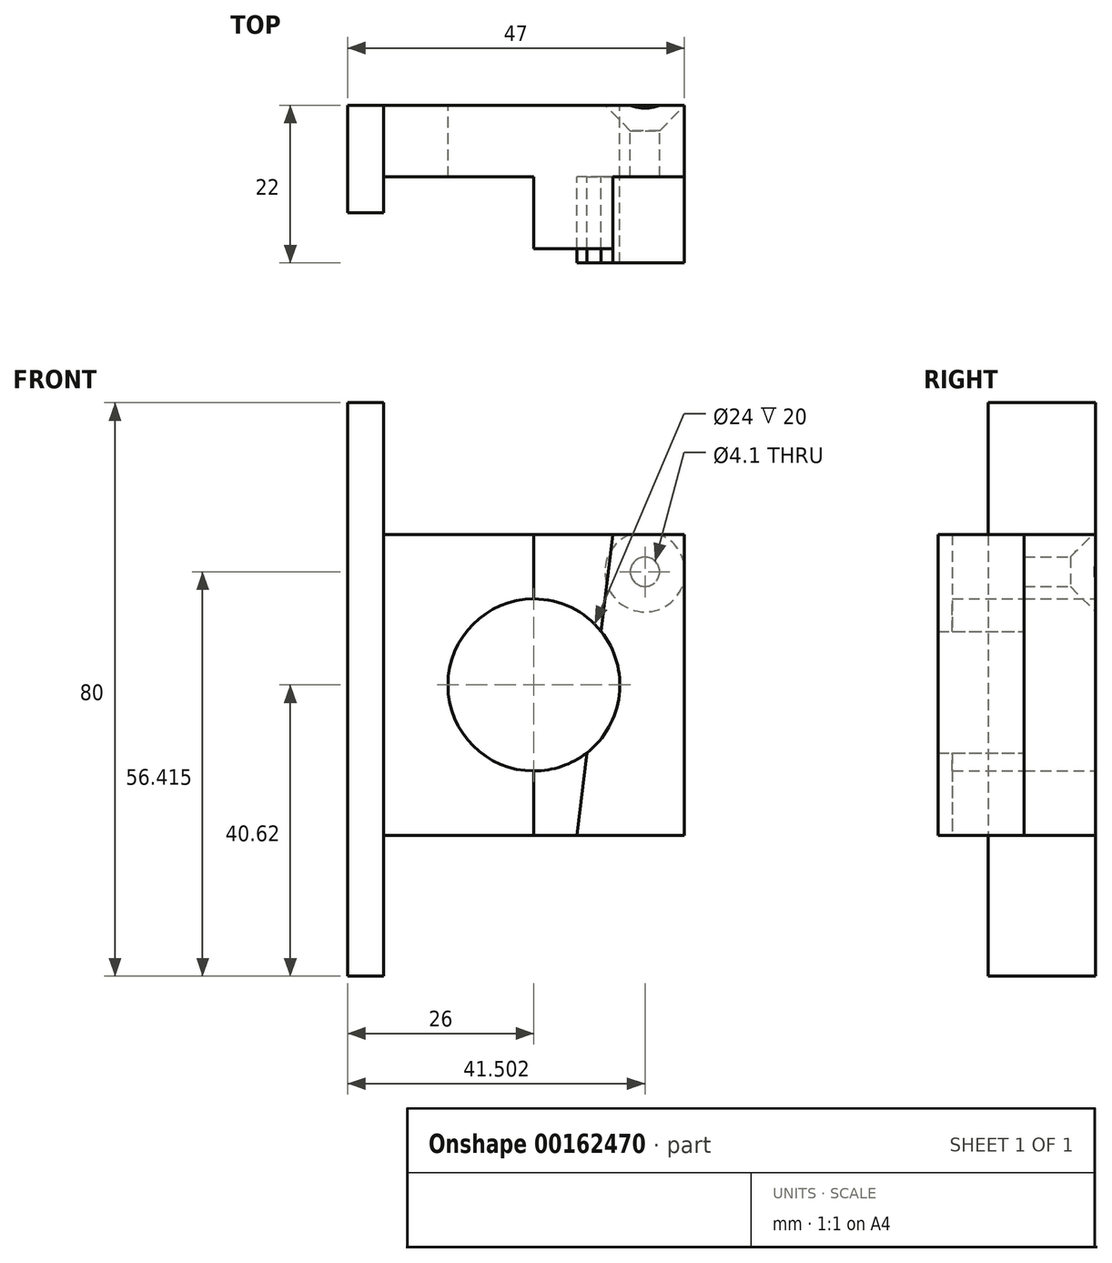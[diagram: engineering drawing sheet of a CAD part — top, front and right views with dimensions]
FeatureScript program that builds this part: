
annotation { "Feature Type Name" : "Feature", "Feature Type Description" : "" }
export const myFeature = defineFeature(function(context is Context, id is Id, definition is map)
    precondition{}
    {
        {
            var Q0;
            Q0=qCreatedBy(makeId("Front.planeOp"),FACE);
            var sketch = newSketch(context, id + "F0", { "sketchPlane" : qUnion([Q0])});
            skLineSegment(sketch, "E0.bottom", {"start": v(21, 21) * mm, "end": v(-21, 21) * mm});
            skLineSegment(sketch, "E0.top", {"start": v(21, -21) * mm, "end": v(-21, -21) * mm});
            skLineSegment(sketch, "E0.left", {"start": v(21, 21) * mm, "end": v(21, -21) * mm});
            skLineSegment(sketch, "E0.right", {"start": v(-21, 21) * mm, "end": v(-21, -21) * mm});
            skPoint(sketch, "E0.middle", {"position": v(0, 0) * mm});
            skCircle(sketch, "E1", {"center": v(0, 0) * mm, "radius": 12 * mm});
            skSolve(sketch);
        }
        {
            var Q0;
            Q0=makeQuery(id+"F0.imprint","IMPRINT",FACE,{"disambiguationData":[TD([[makeQuery(id+"F0.imprint","IMPRINT",EDGE,{"derivedFrom":sQuery(id+"F0.wireOp",EDGE,"E0.bottom")}),1.0]])]});
            extrude(context, id + "F1", {"entities" : qUnion([Q0]), "depth" : 10 * mm});
        }
        {
            var Q0;
            Q0=makeQuery(id+"F1.opExtrude","SWEPT_FACE",FACE,{"disambiguationData":[OSD([sQuery(id+"F0.wireOp",EDGE,"E0.right")])]});
            var sketch = newSketch(context, id + "F2", { "sketchPlane" : qUnion([Q0])});
            skLineSegment(sketch, "E2.bottom", {"start": v(0, 39.38) * mm, "end": v(15, 39.38) * mm});
            skLineSegment(sketch, "E2.top", {"start": v(0, -40.62) * mm, "end": v(15, -40.62) * mm});
            skLineSegment(sketch, "E2.left", {"start": v(0, 39.38) * mm, "end": v(0, -40.62) * mm});
            skLineSegment(sketch, "E2.right", {"start": v(15, 39.38) * mm, "end": v(15, -40.62) * mm});
            skSolve(sketch);
        }
        {
            var Q0;
            Q0 = qSketchRegion(id + "F2", true);
            extrude(context, id + "F3", {"entities" : qUnion([Q0]), "operationType" : NewBodyOperationType.ADD, "depth" : 5 * mm});
        }
        {
            var Q0;
            Q0=makeQuery(id+"F1.opExtrude","CAP_FACE",FACE,{"disambiguationData":[OSD([sQuery(id+"F0.wireOp",EDGE,"E0.bottom"),sQuery(id+"F0.wireOp",EDGE,"E0.top"),sQuery(id+"F0.wireOp",EDGE,"E0.left"),sQuery(id+"F0.wireOp",EDGE,"E0.right"),sQuery(id+"F0.wireOp",EDGE,"E1")])],"isStart":false});
            var sketch = newSketch(context, id + "F4", { "sketchPlane" : qUnion([Q0])});
            skLineSegment(sketch, "E3", {"start": v(11, 21) * mm, "end": v(6, -21) * mm});
            skLineSegment(sketch, "E4", {"start": v(0, 21) * mm, "end": v(0, -21) * mm});
            skSolve(sketch);
        }
        {
            var Q0;
            {var subQ0=sQuery(id+"F4.wireOp",EDGE,"E3");var subQ1=makeQuery(id+"F1.opExtrude","CAP_EDGE",EDGE,{"disambiguationData":[OSD([sQuery(id+"F0.wireOp",EDGE,"E0.bottom")])],"isStart":false});var subQ2=makeQuery(id+"F4.imprint","INTERSECT",VERTEX,{"derivedFrom":[subQ1,subQ0]});Q0=makeQuery(id+"F4.imprint","IMPRINT",FACE,{"disambiguationData":[TD([[makeQuery(id+"F4.imprint","IMPRINT",EDGE,{"disambiguationData":[TD([[subQ2,-1.0]])],"derivedFrom":subQ0}),-1.0]])]});}
            var Q1;
            {var subQ0=sQuery(id+"F4.wireOp",EDGE,"E3");var subQ1=makeQuery(id+"F1.opExtrude","CAP_EDGE",EDGE,{"disambiguationData":[OSD([sQuery(id+"F0.wireOp",EDGE,"E0.top")])],"isStart":false});var subQ2=makeQuery(id+"F4.imprint","INTERSECT",VERTEX,{"derivedFrom":[subQ1,subQ0]});Q1=makeQuery(id+"F4.imprint","IMPRINT",FACE,{"disambiguationData":[TD([[makeQuery(id+"F4.imprint","IMPRINT",EDGE,{"disambiguationData":[TD([[subQ2,1.0]])],"derivedFrom":subQ0}),-1.0]])]});}
            extrude(context, id + "F5", {"entities" : qUnion([Q0, Q1]), "operationType" : NewBodyOperationType.ADD, "depth" : 10 * mm});
        }
        {
            var Q0;
            {var subQ0=sQuery(id+"F0.wireOp",EDGE,"E1");var subQ2=sQuery(id+"F0.wireOp",EDGE,"E0.bottom");var subQ6=sQuery(id+"F0.wireOp",EDGE,"E0.left");var subQ7=sQuery(id+"F0.wireOp",EDGE,"E0.top");Q0=makeQuery(id+"F5.boolean.opBoolean","SPLIT",FACE,{"disambiguationData":[TD([makeQuery(id+"F1.opExtrude","SWEPT_FACE",FACE,{"disambiguationData":[OSD([subQ6])]})])],"derivedFrom":makeQuery(id+"F1.opExtrude","CAP_FACE",FACE,{"disambiguationData":[OSD([subQ2,subQ7,subQ6,sQuery(id+"F0.wireOp",EDGE,"E0.right"),subQ0])],"isStart":false})});}
            extrude(context, id + "F6", {"entities" : qUnion([Q0]), "depth" : 12 * mm});
        }
        {
            var Q0;
            Q0=makeQuery(id+"F3.boolean.opBoolean","MERGE",FACE,{"derivedFrom":[makeQuery(id+"F1.opExtrude","CAP_FACE",FACE,{"disambiguationData":[OSD([sQuery(id+"F0.wireOp",EDGE,"E0.bottom"),sQuery(id+"F0.wireOp",EDGE,"E0.top"),sQuery(id+"F0.wireOp",EDGE,"E0.left"),sQuery(id+"F0.wireOp",EDGE,"E0.right"),sQuery(id+"F0.wireOp",EDGE,"E1")])],"isStart":true}),makeQuery(id+"F3.opExtrude","SWEPT_FACE",FACE,{"disambiguationData":[OSD([sQuery(id+"F2.wireOp",EDGE,"E2.left")])]})]});
            var sketch = newSketch(context, id + "F7", { "sketchPlane" : qUnion([Q0])});
            skPoint(sketch, "E5", {"position": v(-15.5, 15.8) * mm});
            skPoint(sketch, "E6", {"position": v(-15.42, 15.79) * mm});
            skPoint(sketch, "E7", {"position": v(-15.5, 15.72) * mm});
            skSolve(sketch);
        }
        {
            var Q0;
            Q0=sQuery(id+"F7.wireOp",VERTEX,"E5");
            var Q1;
            Q1=makeQuery(id+"F1.opExtrude","SWEPT_BODY",BODY,{"disambiguationData":[OSD([sQuery(id+"F0.wireOp",EDGE,"E0.bottom"),sQuery(id+"F0.wireOp",EDGE,"E0.top"),sQuery(id+"F0.wireOp",EDGE,"E0.left"),sQuery(id+"F0.wireOp",EDGE,"E0.right"),sQuery(id+"F0.wireOp",EDGE,"E1")])]});
            hole(context, id + "F8", {"style" : HoleStyle.C_SINK, "endStyle" : HoleEndStyle.THROUGH, "standardTappedOrClearance" : lookupTablePath({ "standard" : "ISO", "engagement" : "75%", "pitch" : "0.9 mm", "size" : "M5", "type" : "Tapped" }), "standardBlindInLast" : lookupTablePath({ "standard" : "ISO", "engagement" : "75%", "pitch" : "0.9 mm", "size" : "M5", "type" : "Tapped" }), "holeDiameter" : 4.1 * mm, "cSinkDiameter" : 11.2 * mm, "cSinkAngle" : 90 * degree, "locations" : qUnion([Q0]), "scope" : qUnion([Q1]), "isTappedThrough" : true, "showTappedDepth" : true});
        }
    });
